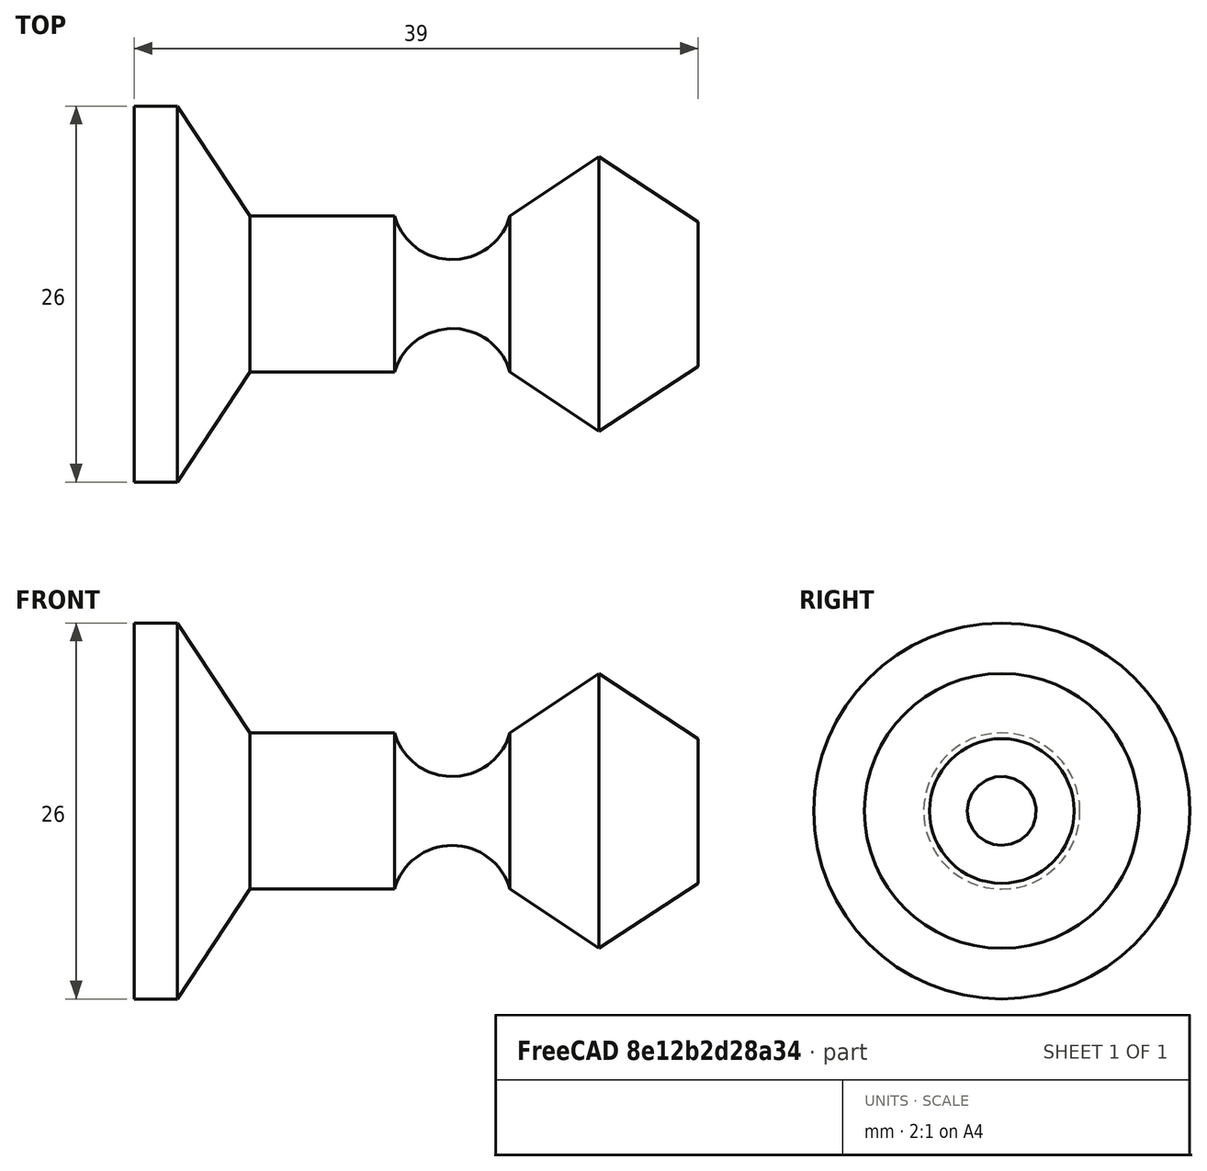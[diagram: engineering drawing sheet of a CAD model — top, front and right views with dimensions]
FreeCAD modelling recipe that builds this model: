
FCSTD DOCUMENT  (FreeCAD 0.21R33678 +9 (Git))
Label: model_test_Profile
License: All rights reserved
LicenseURL: http://en.wikipedia.org/wiki/All_rights_reserved
objects: Sketcher::SketchObject×1, PartDesign::Revolution×1, PartDesign::Body×1
note: 4 computed .brp shape members not serialized (recipe doc carries the construction recipe); baked Part::Feature solids carry a one-line shape summary decoded from their .brp

FEATURE [Sketcher::SketchObject] Sketch
  FullyConstrained = true
  MapMode = 5
  Placement = pos=(0,0,0) rot=(1,0,0;1.5708rad)
  Support = -> [XZ_Plane001]
  sketch-geometry (10):
    g0: LineSegment StartX=-9 StartY=-5 StartZ=0 EndX=-15.85 EndY=-9.5 EndZ=0
    g1: LineSegment StartX=-15.85 StartY=-9.5 StartZ=0 EndX=-22 EndY=-5.4 EndZ=0
    g2: LineSegment StartX=-45 StartY=-13 StartZ=0 EndX=-48 EndY=-13 EndZ=0
    g3: LineSegment StartX=-48 StartY=-13 StartZ=0 EndX=-48 EndY=3.6e-15 EndZ=0
    g4: LineSegment StartX=-48 StartY=4.1e-15 StartZ=0 EndX=10 EndY=4.1e-15 EndZ=0
    g5: ArcOfCircle CenterX=-0.226662 CenterY=0.261315 CenterZ=0 NormalX=0 NormalY=0 NormalZ=1 AngleXU=0 Radius=10.23 StartAngle=3.68179 EndAngle=6.25764
    g6: ArcOfCircle CenterX=-26 CenterY=-6.54263 CenterZ=0 NormalX=0 NormalY=0 NormalZ=1 AngleXU=0 Radius=4.16 StartAngle=0.278247 EndAngle=2.86335
    g7: LineSegment StartX=-30 StartY=-5.4 StartZ=0 EndX=-35 EndY=-5.4 EndZ=0
    g8: LineSegment StartX=-35 StartY=-5.4 StartZ=0 EndX=-40 EndY=-5.4 EndZ=0
    g9: LineSegment StartX=-40 StartY=-5.4 StartZ=0 EndX=-45 EndY=-13 EndZ=0
  constraints (32):
    c: Coincident(g0,g1)
    c: Coincident(g2,g3)
    c: PointOnObject(g3,g-1)
    c: Vertical(g3)
    c: DistanceX(g3) = -48
    c: DistanceY(g3,g3) = 13
    c: DistanceX(g2) = -45
    c: Horizontal(g2)
    c: DistanceX(g0) = -9
    c: DistanceY(g0) = -5
    c: DistanceX(g0) = -15.85
    c: DistanceY(g0) = -9.5
    c: DistanceX(g1) = -22
    c: DistanceY(g1) = -5.4
    c: DistanceX(g6) = -30
    c: Coincident(g4,g3)
    c: Horizontal(g4)
    c: DistanceX(g-1,g4) = 10
    c: Coincident(g5,g4)
    c: Coincident(g5,g0)
    c: Coincident(g6,g1)
    c: Horizontal(g1,g6)
    c: Coincident(g7,g6)
    c: Horizontal(g7)
    c: Coincident(g7,g8)
    c: Horizontal(g8)
    c: Coincident(g8,g9)
    c: Coincident(g9,g2)
    c: DistanceX(g7) = -35
    c: DistanceX(g8) = -40
    c: Radius(g6) = 4.16
    c: Radius(g5) = 10.23
FEATURE [PartDesign::Revolution] Revolution
  Angle = 360
  Axis = (1,0,0)
  Base = (0,0,0)
  Placement = pos=(0,0,0) rot=(1,0,0;1.5708rad)
  Profile = -> Sketch
  ReferenceAxis = -> X_Axis001
  Reversed = true
FEATURE [PartDesign::Body] Body001
  Group = -> [Sketch,Revolution]
  Origin = -> Origin001
  Tip = -> Revolution
